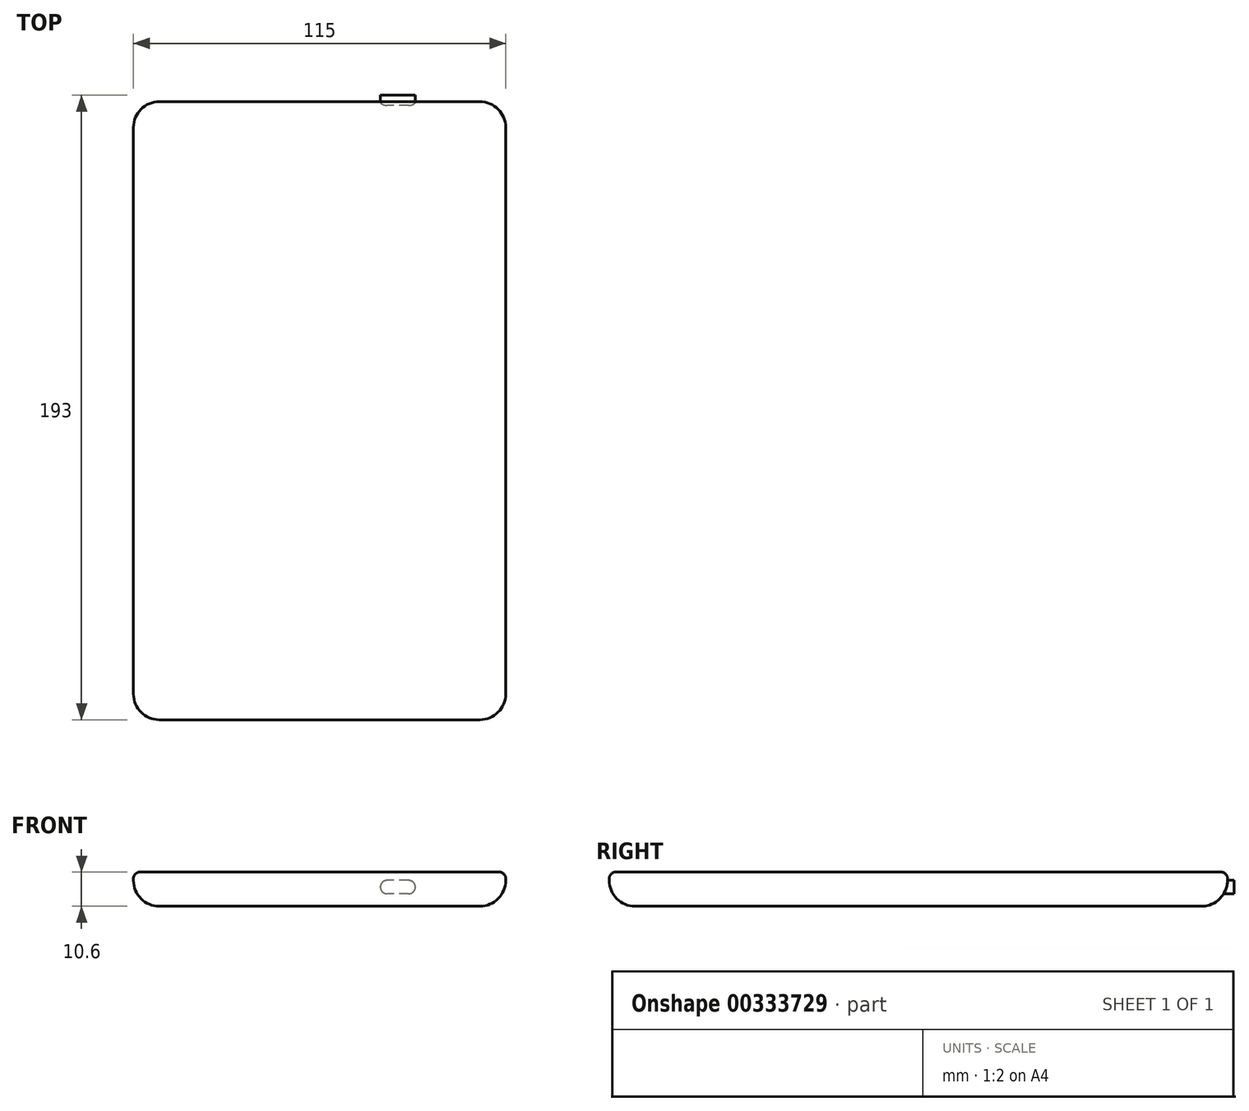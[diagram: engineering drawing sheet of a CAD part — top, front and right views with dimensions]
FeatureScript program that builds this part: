
annotation { "Feature Type Name" : "Feature", "Feature Type Description" : "" }
export const myFeature = defineFeature(function(context is Context, id is Id, definition is map)
    precondition{}
    {
        {
            var Q0;
            Q0=qCreatedBy(makeId("Top.planeOp"),FACE);
            var sketch = newSketch(context, id + "F0", { "sketchPlane" : qUnion([Q0])});
            skLineSegment(sketch, "E0.bottom", {"start": v(57.5, 95.5) * mm, "end": v(-57.5, 95.5) * mm});
            skLineSegment(sketch, "E0.top", {"start": v(57.5, -95.5) * mm, "end": v(-57.5, -95.5) * mm});
            skLineSegment(sketch, "E0.left", {"start": v(57.5, 95.5) * mm, "end": v(57.5, -95.5) * mm});
            skLineSegment(sketch, "E0.right", {"start": v(-57.5, 95.5) * mm, "end": v(-57.5, -95.5) * mm});
            skPoint(sketch, "E0.middle", {"position": v(0, 0) * mm});
            skSolve(sketch);
        }
        {
            var Q0;
            Q0=makeQuery(id+"F0.imprint","IMPRINT",FACE,{"disambiguationData":[TD([[makeQuery(id+"F0.imprint","IMPRINT",EDGE,{"derivedFrom":sQuery(id+"F0.wireOp",EDGE,"E0.bottom")}),1.0]])]});
            extrude(context, id + "F1", {"entities" : qUnion([Q0]), "depth" : 10.6 * mm});
        }
        {
            var Q0;
            Q0=makeQuery(id+"F1.opExtrude","CAP_EDGE",EDGE,{"disambiguationData":[OSD([sQuery(id+"F0.wireOp",EDGE,"E0.right")])],"isStart":true});
            var Q1;
            Q1=makeQuery(id+"F1.opExtrude","CAP_EDGE",EDGE,{"disambiguationData":[OSD([sQuery(id+"F0.wireOp",EDGE,"E0.bottom")])],"isStart":true});
            var Q2;
            Q2=makeQuery(id+"F1.opExtrude","CAP_EDGE",EDGE,{"disambiguationData":[OSD([sQuery(id+"F0.wireOp",EDGE,"E0.left")])],"isStart":true});
            var Q3;
            Q3=makeQuery(id+"F1.opExtrude","CAP_EDGE",EDGE,{"disambiguationData":[OSD([sQuery(id+"F0.wireOp",EDGE,"E0.top")])],"isStart":true});
            var Q4;
            Q4=makeQuery(id+"F1.opExtrude","SWEPT_EDGE",EDGE,{"disambiguationData":[OSD([sQuery(id+"F0.wireOp",EDGE,"E0.bottom"),sQuery(id+"F0.wireOp",EDGE,"E0.right")])]});
            var Q5;
            Q5=makeQuery(id+"F1.opExtrude","SWEPT_EDGE",EDGE,{"disambiguationData":[OSD([sQuery(id+"F0.wireOp",EDGE,"E0.bottom"),sQuery(id+"F0.wireOp",EDGE,"E0.left")])]});
            var Q6;
            Q6=makeQuery(id+"F1.opExtrude","SWEPT_EDGE",EDGE,{"disambiguationData":[OSD([sQuery(id+"F0.wireOp",EDGE,"E0.top"),sQuery(id+"F0.wireOp",EDGE,"E0.left")])]});
            var Q7;
            Q7=makeQuery(id+"F1.opExtrude","SWEPT_EDGE",EDGE,{"disambiguationData":[OSD([sQuery(id+"F0.wireOp",EDGE,"E0.top"),sQuery(id+"F0.wireOp",EDGE,"E0.right")])]});
            fillet(context, id + "F2", {"entities" : qUnion([Q0, Q1, Q2, Q3, Q4, Q5, Q6, Q7]), "radius" : 8 * mm, "tangentPropagation" : true, "allowEdgeOverflow" : false});
        }
        {
            var Q0;
            Q0=makeQuery(id+"F1.opExtrude","CAP_EDGE",EDGE,{"disambiguationData":[OSD([sQuery(id+"F0.wireOp",EDGE,"E0.top")])],"isStart":false});
            fillet(context, id + "F3", {"entities" : qUnion([Q0]), "radius" : 2 * mm, "tangentPropagation" : true, "allowEdgeOverflow" : false});
        }
        {
            var Q0;
            Q0=makeQuery(id+"F1.opExtrude","SWEPT_FACE",FACE,{"disambiguationData":[OSD([sQuery(id+"F0.wireOp",EDGE,"E0.bottom")])]});
            var sketch = newSketch(context, id + "F4", { "sketchPlane" : qUnion([Q0])});
            skLineSegment(sketch, "E1.0", {"start": v(-49.5, 10.6) * mm, "end": v(49.5, 10.6) * mm, "construction": true});
            skPoint(sketch, "E2.0", {"position": v(-57.5, 8.6) * mm});
            skLineSegment(sketch, "E3.bottom", {"start": v(-18.8, 8.45) * mm, "end": v(-29.55, 8.45) * mm});
            skLineSegment(sketch, "E3.top", {"start": v(-18.8, 3.85) * mm, "end": v(-29.55, 3.85) * mm});
            skLineSegment(sketch, "E3.left", {"start": v(-18.8, 8.45) * mm, "end": v(-18.8, 3.85) * mm});
            skLineSegment(sketch, "E3.right", {"start": v(-29.55, 8.45) * mm, "end": v(-29.55, 3.85) * mm});
            skPoint(sketch, "E3.middle", {"position": v(-24.17, 6.15) * mm});
            skSolve(sketch);
        }
        {
            var Q0;
            {var subQ0=sQuery(id+"F4.wireOp",EDGE,"E3.top");Q0=makeQuery(id+"F4.imprint","IMPRINT",FACE,{"disambiguationData":[TD([[makeQuery(id+"F4.imprint","IMPRINT",EDGE,{"derivedFrom":subQ0}),-1.0]])]});}
            extrude(context, id + "F5", {"entities" : qUnion([Q0]), "operationType" : NewBodyOperationType.ADD, "oppositeDirection" : true, "depth" : 2 * mm, "offsetDistance" : 25 * mm});
        }
        {
            var Q0;
            {var subQ0=sQuery(id+"F4.wireOp",EDGE,"E3.top");Q0=makeQuery(id+"F4.imprint","IMPRINT",FACE,{"disambiguationData":[TD([[makeQuery(id+"F4.imprint","IMPRINT",EDGE,{"derivedFrom":subQ0}),-1.0]])]});}
            extrude(context, id + "F6", {"entities" : qUnion([Q0]), "operationType" : NewBodyOperationType.ADD, "offsetDistance" : 25 * mm, "depth" : 2 * mm});
        }
        {
            var Q0;
            Q0=makeQuery(id+"F6.opExtrude","SWEPT_EDGE",EDGE,{"disambiguationData":[OSD([sQuery(id+"F0.wireOp",EDGE,"E0.bottom"),sQuery(id+"F4.wireOp",EDGE,"E3.left")])]});
            var Q1;
            Q1=makeQuery(id+"F6.opExtrude","SWEPT_EDGE",EDGE,{"disambiguationData":[OSD([sQuery(id+"F4.wireOp",EDGE,"E3.top"),sQuery(id+"F4.wireOp",EDGE,"E3.left")])]});
            var Q2;
            Q2=makeQuery(id+"F6.opExtrude","SWEPT_EDGE",EDGE,{"disambiguationData":[OSD([sQuery(id+"F4.wireOp",EDGE,"E3.top"),sQuery(id+"F4.wireOp",EDGE,"E3.right")])]});
            var Q3;
            Q3=makeQuery(id+"F6.opExtrude","SWEPT_EDGE",EDGE,{"disambiguationData":[OSD([sQuery(id+"F0.wireOp",EDGE,"E0.bottom"),sQuery(id+"F4.wireOp",EDGE,"E3.right")])]});
            fillet(context, id + "F7", {"entities" : qUnion([Q0, Q1, Q2, Q3]), "radius" : 2 * mm, "tangentPropagation" : true, "allowEdgeOverflow" : false});
        }
    });
